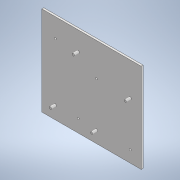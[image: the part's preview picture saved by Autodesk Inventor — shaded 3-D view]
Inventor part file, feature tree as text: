
AUTODESK INVENTOR PART (.ipt)
format: ipt  version: 2020.2 (Build 242310000, 310)  size: 128,512 bytes
history: native  units: mm
features: reference x12, other x4, extrude x3, sketch x3
ambient origin geometry x8: Origin, YZ Plane, XZ Plane, XY Plane, X Axis, Y Axis, Z Axis, Center Point
bodies: Solid1 (feature_tree)
feature tree (22):
  extrude  "Extrusion1"  Depth=90.0mm
  extrude  "Extrusion2"  Depth=2.0mm
  extrude  "Extrusion3"  Depth=2.0mm
  sketch  "Sketch1"  dims[d0=100.0mm d1=90.0mm]
  sketch  "Sketch2"  dims[d2=2.0mm d3=0.0mm d4=2.0mm]
  reference  "Reference1"
  reference  "Reference2"
  reference  "Reference3"
  reference  "Reference4"
  reference  "Reference5"
  reference  "Reference6"
  reference  "Reference7"
  reference  "Reference8"
  sketch  "Sketch3"  dims[d5=2.0mm d6=2.0mm d7=2.0mm d8=2.0mm d9=2.0mm d10=2.0mm d11=2.0mm d12=10.0mm d13=0.0mm d14=0.15mm d15=0.15mm d16=0.15mm d17=0.15mm d18=5.0mm d19=0.0mm]
  reference  "Reference9"
  reference  "Reference10"
  reference  "Reference11"
  reference  "Reference12"
  other  "<userpath>\OneDrive\Apps\0011_VentControlValve\Assembly.iam"
  other  "Assembly.iam"
  other  "Dual Relay w Breakout Board:1"
  other  "RaspberryPiZeroW:1"
